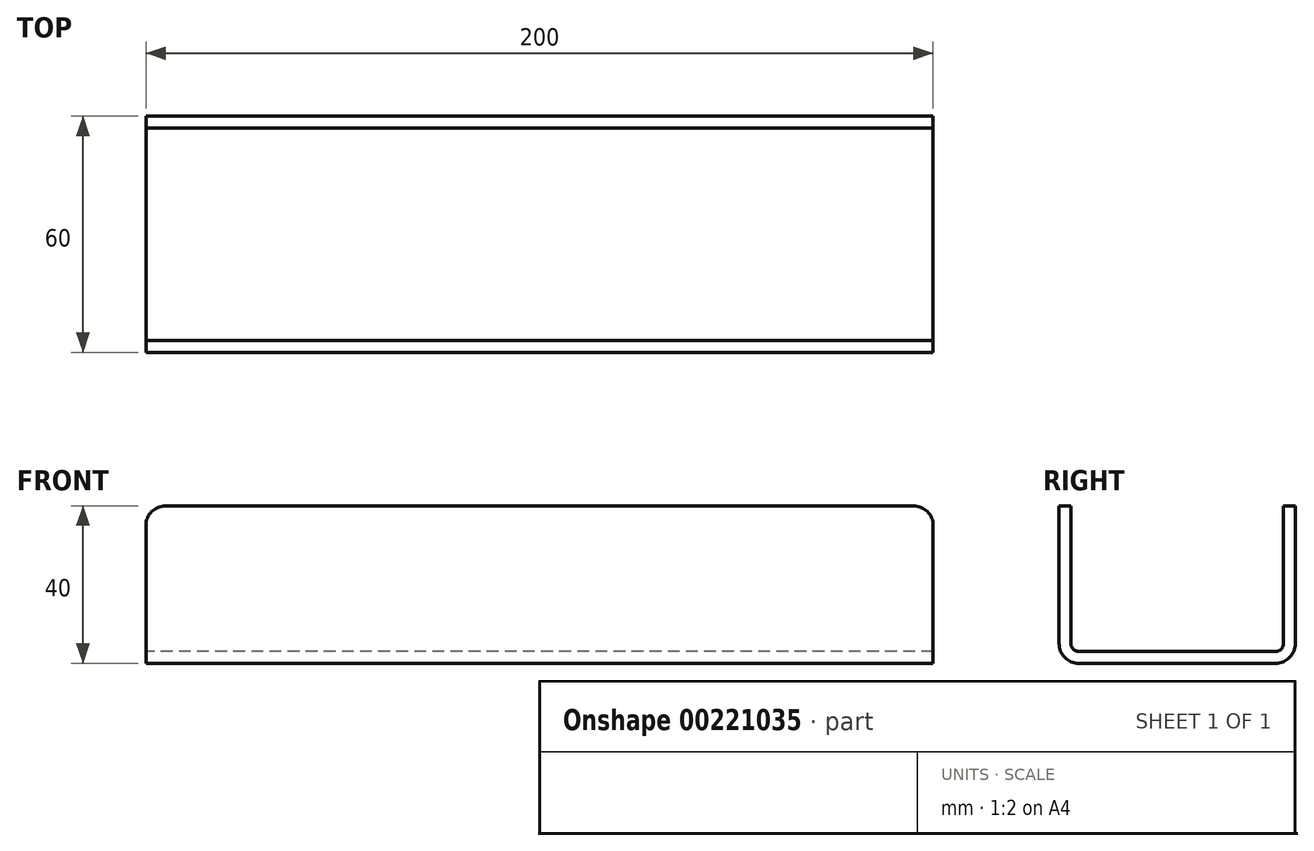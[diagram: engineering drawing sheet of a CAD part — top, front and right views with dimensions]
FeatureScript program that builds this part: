
annotation { "Feature Type Name" : "Feature", "Feature Type Description" : "" }
export const myFeature = defineFeature(function(context is Context, id is Id, definition is map)
    precondition{}
    {
        {
            var Q0;
            Q0=qCreatedBy(makeId("Right.planeOp"),FACE);
            var sketch = newSketch(context, id + "F0", { "sketchPlane" : qUnion([Q0])});
            skLineSegment(sketch, "E0.bottom", {"start": v(30, 20) * mm, "end": v(-30, 20) * mm});
            skLineSegment(sketch, "E0.top", {"start": v(30, -20) * mm, "end": v(-30, -20) * mm});
            skLineSegment(sketch, "E0.left", {"start": v(30, 20) * mm, "end": v(30, -20) * mm});
            skLineSegment(sketch, "E0.right", {"start": v(-30, 20) * mm, "end": v(-30, -20) * mm});
            skPoint(sketch, "E0.middle", {"position": v(0, 0) * mm});
            skSolve(sketch);
        }
        {
            var Q0;
            Q0=makeQuery(id+"F0.imprint","IMPRINT",FACE,{"disambiguationData":[TD([[makeQuery(id+"F0.imprint","IMPRINT",EDGE,{"derivedFrom":sQuery(id+"F0.wireOp",EDGE,"E0.bottom")}),1.0]])]});
            extrude(context, id + "F1", {"entities" : qUnion([Q0]), "endBound" : BoundingType.SYMMETRIC, "depth" : 200 * mm});
        }
        {
            var Q0;
            Q0=makeQuery(id+"F1.opExtrude","SWEPT_EDGE",EDGE,{"disambiguationData":[OSD([sQuery(id+"F0.wireOp",EDGE,"E0.top"),sQuery(id+"F0.wireOp",EDGE,"E0.right")])]});
            var Q1;
            Q1=makeQuery(id+"F1.opExtrude","SWEPT_EDGE",EDGE,{"disambiguationData":[OSD([sQuery(id+"F0.wireOp",EDGE,"E0.top"),sQuery(id+"F0.wireOp",EDGE,"E0.left")])]});
            fillet(context, id + "F2", {"entities" : qUnion([Q0, Q1]), "radius" : 5 * mm, "tangentPropagation" : true, "allowEdgeOverflow" : false});
        }
        {
            var Q0;
            Q0=makeQuery(id+"F1.opExtrude","SWEPT_FACE",FACE,{"disambiguationData":[OSD([sQuery(id+"F0.wireOp",EDGE,"E0.bottom")])]});
            var Q1;
            Q1=makeQuery(id+"F1.opExtrude","CAP_FACE",FACE,{"disambiguationData":[OSD([sQuery(id+"F0.wireOp",EDGE,"E0.bottom"),sQuery(id+"F0.wireOp",EDGE,"E0.top"),sQuery(id+"F0.wireOp",EDGE,"E0.left"),sQuery(id+"F0.wireOp",EDGE,"E0.right")])],"isStart":false});
            var Q2;
            Q2=makeQuery(id+"F1.opExtrude","CAP_FACE",FACE,{"disambiguationData":[OSD([sQuery(id+"F0.wireOp",EDGE,"E0.bottom"),sQuery(id+"F0.wireOp",EDGE,"E0.top"),sQuery(id+"F0.wireOp",EDGE,"E0.left"),sQuery(id+"F0.wireOp",EDGE,"E0.right")])],"isStart":true});
            shell(context, id + "F3", {"entities" : qUnion([Q0, Q1, Q2]), "thickness" : 3 * mm});
        }
        {
            var Q0;
            {var subQ0=sQuery(id+"F0.wireOp",EDGE,"E0.bottom");Q0=makeQuery(id+"F3.opShell","OFFSET_EDGE",EDGE,{"disambiguationData":[OSD([subQ0]),TDD([makeQuery(id+"F1.opExtrude","CAP_EDGE",EDGE,{"disambiguationData":[OSD([subQ0])],"isStart":true})])]});}
            var Q1;
            Q1=makeQuery(id+"F1.opExtrude","CAP_EDGE",EDGE,{"disambiguationData":[OSD([sQuery(id+"F0.wireOp",EDGE,"E0.bottom")])],"isStart":true});
            var Q2;
            {var subQ0=sQuery(id+"F0.wireOp",EDGE,"E0.bottom");Q2=makeQuery(id+"F3.opShell","OFFSET_EDGE",EDGE,{"disambiguationData":[OSD([subQ0]),TDD([makeQuery(id+"F1.opExtrude","CAP_EDGE",EDGE,{"disambiguationData":[OSD([subQ0])],"isStart":false})])]});}
            var Q3;
            Q3=makeQuery(id+"F1.opExtrude","CAP_EDGE",EDGE,{"disambiguationData":[OSD([sQuery(id+"F0.wireOp",EDGE,"E0.bottom")])],"isStart":false});
            fillet(context, id + "F4", {"entities" : qUnion([Q0, Q1, Q2, Q3]), "radius" : 5 * mm, "tangentPropagation" : true, "allowEdgeOverflow" : false});
        }
    });
